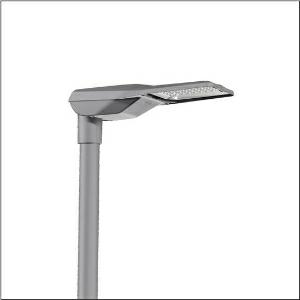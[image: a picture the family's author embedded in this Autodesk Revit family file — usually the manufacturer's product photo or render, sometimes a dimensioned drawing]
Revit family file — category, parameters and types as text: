
# Revit family: streetlight_sl_21_iq_mini___p0_5a_5xe2v31d08jb_3bf9
name_source: partatom
category: Lighting Fixtures
units: mm (PartAtom-declared; Revit-internal decimal feet)

## family parameters
Cut with Voids When Loaded = No
Host = Face
Light Source = No
Part Type = Normal
Room Calculation Point = No
Round Connector Dimension = Use Diameter
Shared = No

## types (1)
- --- (1 x LED, 10640 lm, 71.6 W, 3000K)
    Apparent Load = 72 VA
    CIE Flux Codes = 37 73 96 100 100
    Color Rendering = 70
    Color Temperature = 3000K
    Default Elevation = 1800 mm
    Description = Streetlight SL 21 iQ mini, mast luminaire, primary light control with lens, of PMMA, primary optical cover: cover, of toughened safety glass, transparent, light distribution: P0.5a, light emission: direct distribution, primary light characteristic: asymmetric, installation type: post-top, side-entry, LED, High Power LED, rated luminous flux: 10.640lm, luminous efficacy: 149lm/W, light colour: 730, colour temperature: 3000K, control gear: iQ-Comfort, control: pre-setting: linear dimming characteristic, Auto-Match, Temp-Guard, Lumen-Switch, Night-Set, Smart-Wire, Light-Fading, Desk-Remote (wireless, voltage-free reading and setting of iQ features in the workshop via application-optimized NFC function/RFID function), optimised constant luminous flux control (CLO 2.0), mains connection: 220..240V, AC, 50/60Hz, start of lifetime: 72W, end of service life: 75W, reduction: 33W, luminaire housing, of diecast aluminium, powder-coated, SITECO metallic grey (DB 702S), corrosivity category C5 high according to DIN EN ISO 12944, please order mast flange separately, inclination adjustable: 0°, 5°, 10°, 15°, sealing non-destructively replaceable, multi-level sealing system, length: 628mm, width: 235mm, height: 110mm, mast flange for spigot size: 42mm (side-entry): 5XC10008XM4, 60/48mm (side-entry/post-top): 5XC10108XM2, 76/60mm (side-entry/post-top): 5XC10108XM1, mounting height: 4..8m, protection rating (complete): IP66, insulation class (complete): insulation class II (safety insulation), certification: CE, ENEC, ENEC+, VDE, impact resistance: IK10, permissible operating ambient temperature for outdoor applications: -40..+50°C, standard-compliant lighting for roads and squares, packaging unit: 1 piece

Light Distribution: P0.5a
    Height = 110 mm
    Lamp = 1 x LED
    Lamp Light Flux = 10640 lm
    Lamp Power = 71.6 W
    Lamp count = 1
    Length = 625 mm
    Luminous efficacy = 149 lm/W
    Manufacturer = Siteco
    ModVariant = No
    Model = 5XE2V31D08JB
    Number of Poles = 1
    OnlyDefault = Yes
    Power Factor = 1
    Product Name = Streetlight SL 21 iQ mini | P0.5a
    Product group = mast luminaire | pylon top
    ProductGroupID = 6100
    Protection Class = Protection class II
    Protection Degree = IP 66
    RLX_Detail_Level = 1
    RLX_Emergency_Light_Flux = 0 lm
    RLX_Emergency_Type = 0
    RLX_Emergency_Type_DB = No
    RlxData = <blob elided: 93881 chars, md5=b77f9191>
    Socket = socket
    Standby Power = 0 W
    System Light Flux = 10640 lm
    System Power = 72 W
    Type Comments = factory setting: luminous flux: 100 % | dim-lin: 254 | 746 mA
    Type Image = l_1003519.jpg
    URL = http://relux.com
    VarID = @adj_076977
    Voltage = 0 V
    Weight = 0.00 kg
    Width = 234 mm

## geometry (parser evidence)
native form markers: Blend x4, Sweep x13
no freeform markers — native parametric forms only
